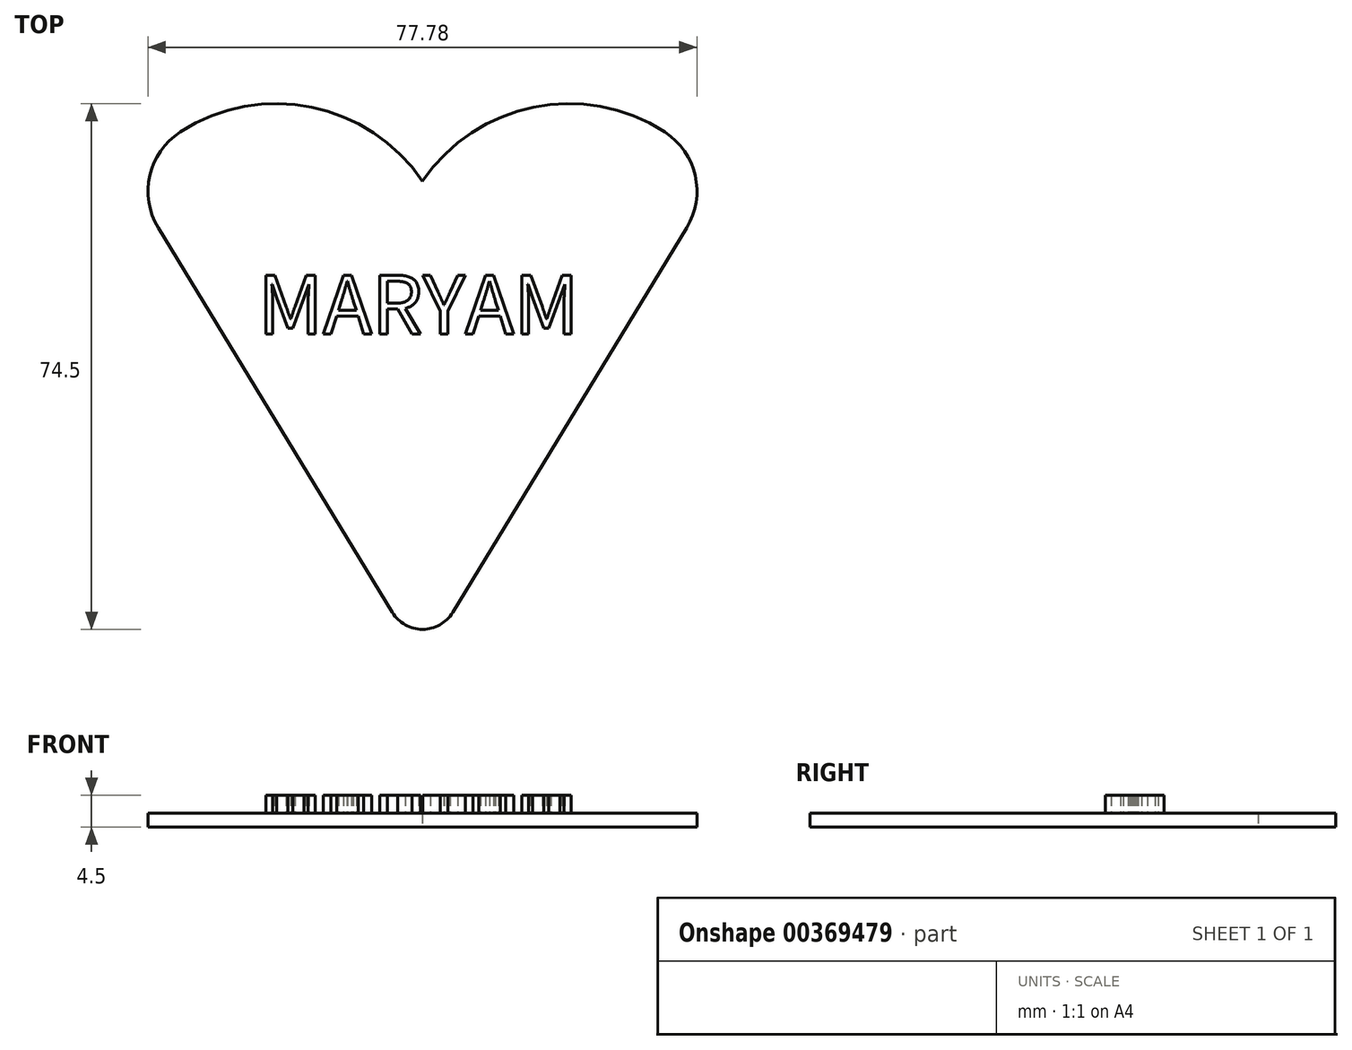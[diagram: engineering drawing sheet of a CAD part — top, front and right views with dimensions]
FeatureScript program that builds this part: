
annotation { "Feature Type Name" : "Feature", "Feature Type Description" : "" }
export const myFeature = defineFeature(function(context is Context, id is Id, definition is map)
    precondition{}
    {
        {
            var Q0;
            Q0=qCreatedBy(makeId("Top.planeOp"),FACE);
            var sketch = newSketch(context, id + "F0", { "sketchPlane" : qUnion([Q0])});
            skArc(sketch, "E0", {"start": v(34.33, 6.99) * mm, "mid": v(15.74, 10.51) * mm, "end": v(0, 0) * mm});
            skLineSegment(sketch, "E1", {"start": v(0, 22.5) * mm, "end": v(0, -28.13) * mm, "construction": true});
            skArc(sketch, "E2.MirrorCS", {"start": v(-34.33, 6.99) * mm, "mid": v(-15.74, 10.51) * mm, "end": v(0, 0) * mm});
            skLineSegment(sketch, "E3", {"start": v(-37.43, -6.6) * mm, "end": v(-4.27, -61.08) * mm});
            skLineSegment(sketch, "E4", {"start": v(4.27, -61.08) * mm, "end": v(37.43, -6.6) * mm});
            skPoint(sketch, "E5.visualSharp", {"position": v(-41.45, 0) * mm});
            skArc(sketch, "E5.filletArc", {"start": v(-34.33, 6.99) * mm, "mid": v(-38.64, 0.82) * mm, "end": v(-37.43, -6.6) * mm});
            skPoint(sketch, "E6.visualSharp", {"position": v(41.45, 0) * mm});
            skArc(sketch, "E6.filletArc", {"start": v(37.43, -6.6) * mm, "mid": v(38.64, 0.82) * mm, "end": v(34.33, 6.99) * mm});
            skPoint(sketch, "E7.visualSharp", {"position": v(0, -68.1) * mm});
            skArc(sketch, "E7.filletArc", {"start": v(-4.27, -61.08) * mm, "mid": v(0, -63.48) * mm, "end": v(4.27, -61.08) * mm});
            skSolve(sketch);
        }
        {
            var Q0;
            Q0 = qSketchRegion(id + "F0", true);
            extrude(context, id + "F1", {"entities" : qUnion([Q0]), "depth" : 2 * mm});
        }
        {
            var Q0;
            Q0=makeQuery(id+"F1.opExtrude","CAP_FACE",FACE,{"disambiguationData":[OSD([sQuery(id+"F0.wireOp",EDGE,"E0"),sQuery(id+"F0.wireOp",EDGE,"E2.MirrorCS"),sQuery(id+"F0.wireOp",EDGE,"E3"),sQuery(id+"F0.wireOp",EDGE,"E4"),sQuery(id+"F0.wireOp",EDGE,"E5.filletArc"),sQuery(id+"F0.wireOp",EDGE,"E6.filletArc"),sQuery(id+"F0.wireOp",EDGE,"E7.filletArc")])],"isStart":false});
            var sketch = newSketch(context, id + "F2", { "sketchPlane" : qUnion([Q0])});
            skText(sketch, "E8", { "text": "MARYAM", "fontName": "NotoSansCJKjp-Regular.otf"});
            const initialGuessF2  = {"E8": [-0.02331, -0.02163, 1, 0, 0.00818]};
            skSetInitialGuess(sketch, initialGuessF2);
            skSolve(sketch);
        }
        {
            var Q0;
            Q0 = qSketchRegion(id + "F2", true);
            extrude(context, id + "F3", {"entities" : qUnion([Q0]), "operationType" : NewBodyOperationType.ADD, "depth" : 2.5 * mm});
        }
    });
